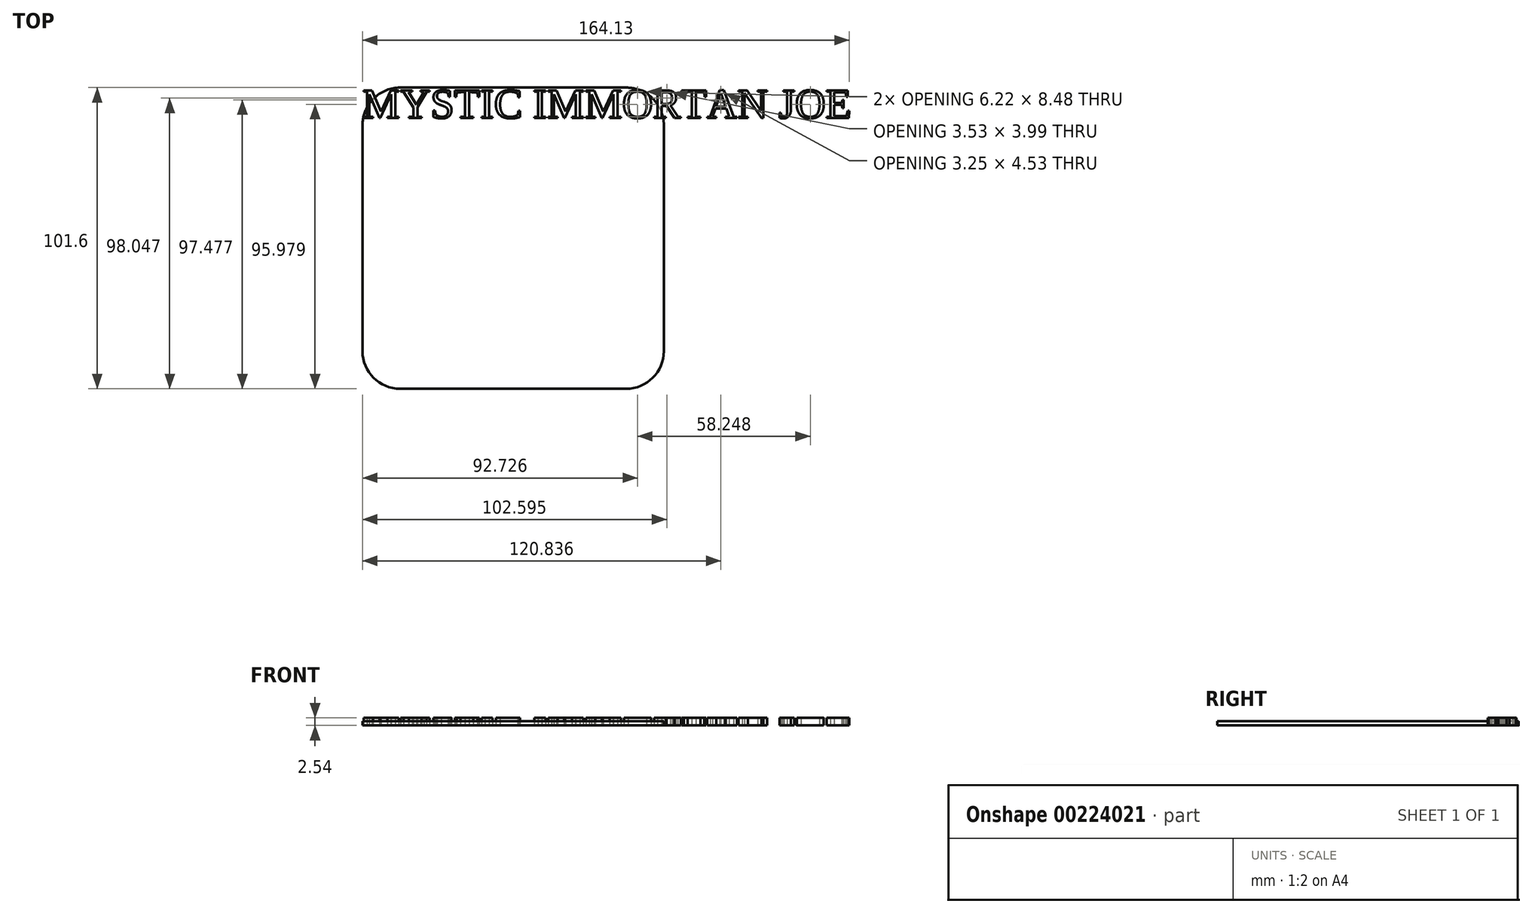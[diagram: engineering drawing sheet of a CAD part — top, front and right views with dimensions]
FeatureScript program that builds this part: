
annotation { "Feature Type Name" : "Feature", "Feature Type Description" : "" }
export const myFeature = defineFeature(function(context is Context, id is Id, definition is map)
    precondition{}
    {
        {
            var Q0;
            Q0=qCreatedBy(makeId("Top.planeOp"),FACE);
            var sketch = newSketch(context, id + "F0", { "sketchPlane" : qUnion([Q0])});
            skLineSegment(sketch, "E0.bottom", {"start": v(12.7, 0) * mm, "end": v(88.9, 0) * mm});
            skLineSegment(sketch, "E0.top", {"start": v(12.7, -101.6) * mm, "end": v(88.9, -101.6) * mm});
            skLineSegment(sketch, "E0.left", {"start": v(0, -12.7) * mm, "end": v(0, -88.9) * mm});
            skLineSegment(sketch, "E0.right", {"start": v(101.6, -12.7) * mm, "end": v(101.6, -88.9) * mm});
            skPoint(sketch, "E1.visualSharp", {"position": v(0, 0) * mm});
            skArc(sketch, "E1.filletArc", {"start": v(12.7, 0) * mm, "mid": v(3.72, -3.72) * mm, "end": v(0, -12.7) * mm});
            skPoint(sketch, "E2.visualSharp", {"position": v(101.6, 0) * mm});
            skArc(sketch, "E2.filletArc", {"start": v(101.6, -12.7) * mm, "mid": v(97.88, -3.72) * mm, "end": v(88.9, 0) * mm});
            skPoint(sketch, "E3.visualSharp", {"position": v(101.6, -101.6) * mm});
            skArc(sketch, "E3.filletArc", {"start": v(88.9, -101.6) * mm, "mid": v(97.88, -97.88) * mm, "end": v(101.6, -88.9) * mm});
            skPoint(sketch, "E4.visualSharp", {"position": v(0, -101.6) * mm});
            skArc(sketch, "E4.filletArc", {"start": v(0, -88.9) * mm, "mid": v(3.72, -97.88) * mm, "end": v(12.7, -101.6) * mm});
            skSolve(sketch);
        }
        {
            var Q0;
            Q0 = qSketchRegion(id + "F0", true);
            extrude(context, id + "F1", {"entities" : qUnion([Q0]), "depth" : 1.5 * mm});
        }
        {
            var Q0;
            Q0=qCreatedBy(makeId("Top.planeOp"),FACE);
            var sketch = newSketch(context, id + "F2", { "sketchPlane" : qUnion([Q0])});
            skText(sketch, "E5", { "text": "MYSTIC IMMORTAN JOE", "fontName": "Tinos-Regular.ttf"});
            const initialGuessF2  = {"E5": [0, -0.01027, 1, 0, 0.01027]};
            skSetInitialGuess(sketch, initialGuessF2);
            skSolve(sketch);
        }
        {
            var Q0;
            Q0 = qSketchRegion(id + "F2", true);
            extrude(context, id + "F3", {"entities" : qUnion([Q0]), "depth" : 2.54 * mm});
        }
    });
